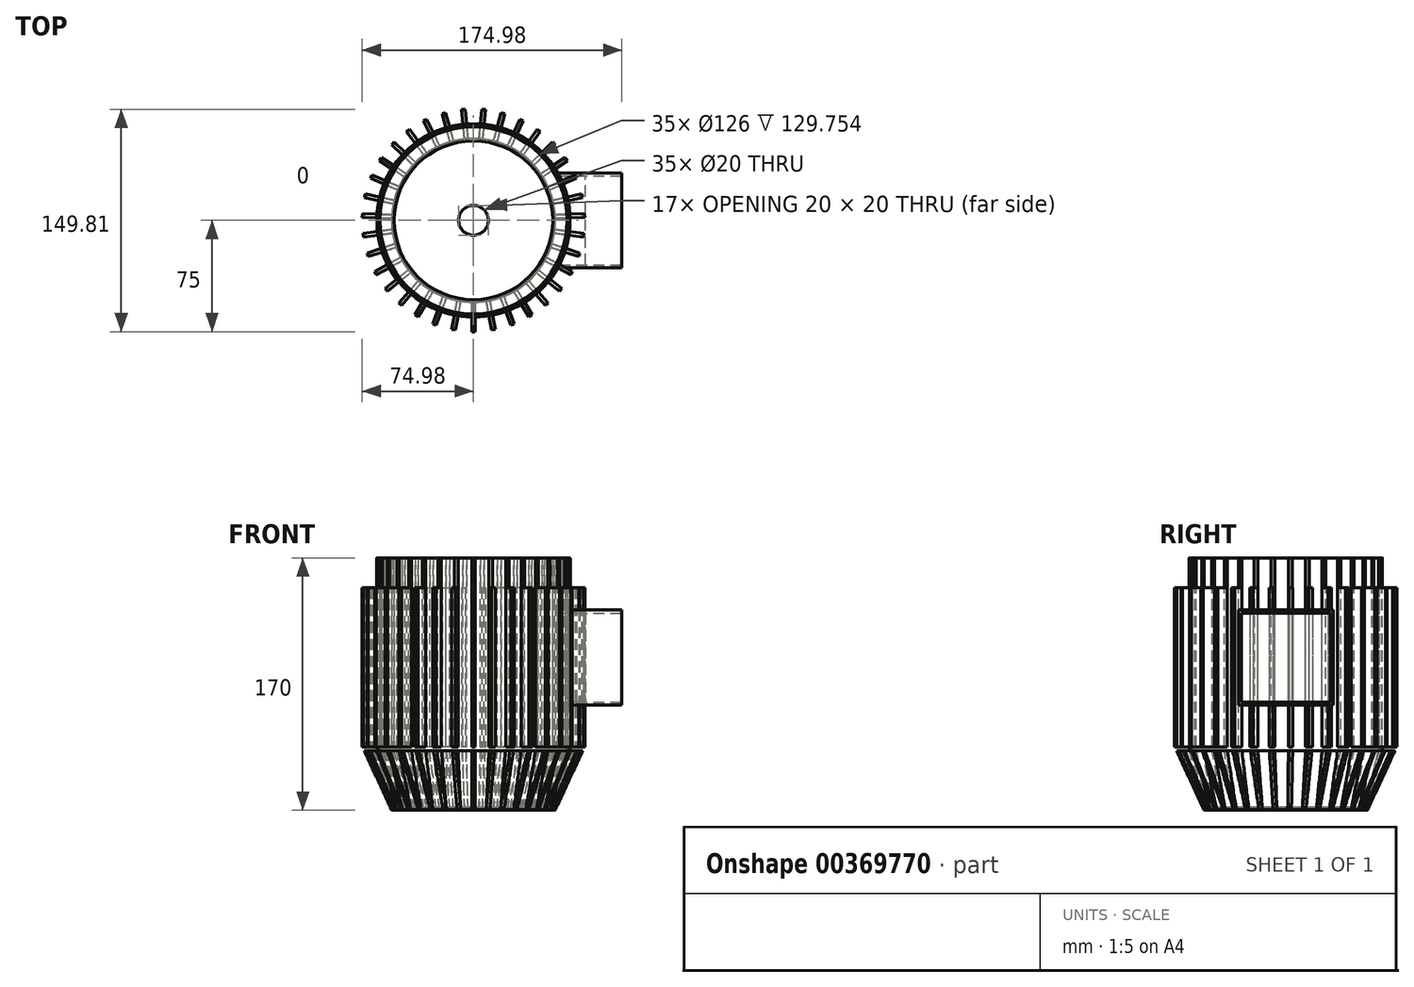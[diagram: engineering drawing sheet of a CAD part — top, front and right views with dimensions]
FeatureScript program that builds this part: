
annotation { "Feature Type Name" : "Feature", "Feature Type Description" : "" }
export const myFeature = defineFeature(function(context is Context, id is Id, definition is map)
    precondition{}
    {
        {
            var Q0;
            Q0=qCreatedBy(makeId("Top.planeOp"),FACE);
            var sketch = newSketch(context, id + "F0", { "sketchPlane" : qUnion([Q0])});
            skCircle(sketch, "E0", {"center": v(0, 0) * mm, "radius": 65 * mm});
            skSolve(sketch);
        }
        {
            var Q0;
            Q0=makeQuery(id+"F0.imprint","IMPRINT",FACE,{"disambiguationData":[TD([[makeQuery(id+"F0.imprint","IMPRINT",EDGE,{"derivedFrom":sQuery(id+"F0.wireOp",EDGE,"E0")}),1.0]])]});
            extrude(context, id + "F1", {"entities" : qUnion([Q0]), "oppositeDirection" : true, "depth" : 170 * mm, "offsetDistance" : 25 * mm});
        }
        {
            var Q0;
            Q0=makeQuery(id+"F1.opExtrude","CAP_FACE",FACE,{"disambiguationData":[OSD([sQuery(id+"F0.wireOp",EDGE,"E0")])],"isStart":false});
            chamfer(context, id + "F2", {"entities" : qUnion([Q0]), "chamferType" : ChamferType.TWO_OFFSETS, "width1" : 10 * mm, "oppositeDirection" : true, "width2" : 40 * mm, "tangentPropagation" : true});
        }
        {
            var Q0;
            Q0=makeQuery(id+"F1.opExtrude","CAP_FACE",FACE,{"disambiguationData":[OSD([sQuery(id+"F0.wireOp",EDGE,"E0")])],"isStart":true});
            shell(context, id + "F3", {"entities" : qUnion([Q0]), "thickness" : 2 * mm});
        }
        {
            var Q0;
            Q0=qCreatedBy(makeId("Front.planeOp"),FACE);
            cPlane(context, id + "F4", {"entities" : qUnion([Q0]), "cplaneType" : CPlaneType.OFFSET, "offset" : 75 * mm, "width" : 150 * mm, "height" : 150 * mm});
        }
        {
            var Q0;
            Q0=qCreatedBy(id+"F4.planeOp",FACE);
            var sketch = newSketch(context, id + "F5", { "sketchPlane" : qUnion([Q0])});
            skLineSegment(sketch, "E1.bottom", {"start": v(-1.25, 0) * mm, "end": v(1.25, 0) * mm});
            skLineSegment(sketch, "E1.top", {"start": v(-1.25, -170) * mm, "end": v(1.25, -170) * mm});
            skLineSegment(sketch, "E1.left", {"start": v(-1.25, 0) * mm, "end": v(-1.25, -170) * mm});
            skLineSegment(sketch, "E1.right", {"start": v(1.25, 0) * mm, "end": v(1.25, -170) * mm});
            skPoint(sketch, "E2.endSnap0", {"position": v(0, 0) * mm});
            skSolve(sketch);
        }
        {
            var Q0;
            Q0 = qSketchRegion(id + "F5", true);
            extrude(context, id + "F6", {"entities" : qUnion([Q0]), "operationType" : NewBodyOperationType.ADD, "endBound" : BoundingType.UP_TO_NEXT, "oppositeDirection" : true, "depth" : 22.5 * mm, "offsetDistance" : 25 * mm});
        }
        {
            var Q0;
            Q0=makeQuery(id+"F1.opExtrude","SWEPT_BODY",BODY,{"disambiguationData":[OSD([sQuery(id+"F0.wireOp",EDGE,"E0")])]});
            var Q1;
            Q1=makeQuery(id+"F1.opExtrude","SWEPT_FACE",FACE,{"disambiguationData":[OSD([sQuery(id+"F0.wireOp",EDGE,"E0")])]});
            circularPattern(context, id + "F7", {"entities" : qUnion([Q0]), "axis" : qUnion([Q1]), "angle" : 360 * degree, "instanceCount" : 35, "equalSpace" : true});
        }
        {
            var Q0;
            Q0=qCreatedBy(makeId("Front.planeOp"),FACE);
            var sketch = newSketch(context, id + "F8", { "sketchPlane" : qUnion([Q0])});
            skLineSegment(sketch, "E3", {"start": v(-54.94, -169.96) * mm, "end": v(-73.62, -129.74) * mm});
            skLineSegment(sketch, "E4", {"start": v(-80.72, -176.26) * mm, "end": v(-80.72, -127.24) * mm});
            skLineSegment(sketch, "E5", {"start": v(-80.72, -127.24) * mm, "end": v(-65, -127.24) * mm});
            skLineSegment(sketch, "E6", {"start": v(-73.62, -129.74) * mm, "end": v(-65, -129.74) * mm});
            skLineSegment(sketch, "E7", {"start": v(-65, -129.74) * mm, "end": v(-65, -127.24) * mm});
            skLineSegment(sketch, "E8", {"start": v(-80.72, -176.26) * mm, "end": v(-54.94, -169.96) * mm});
            skLineSegment(sketch, "E9", {"start": v(0, -180.24) * mm, "end": v(0, 21.57) * mm, "construction": true});
            skSolve(sketch);
        }
        {
            var Q0;
            Q0 = qSketchRegion(id + "F8", true);
            var Q1;
            Q1=sQuery(id+"F8.wireOp",EDGE,"E9");
            var Q2;
            Q2=sQuery(id+"F8.wireOp",EDGE,"E9");
            revolve(context, id + "F9", {"operationType" : NewBodyOperationType.REMOVE, "entities" : qUnion([Q0]), "surfaceEntities" : qUnion([Q1]), "axis" : qUnion([Q2]), "revolveType" : RevolveType.FULL, "oppositeDirection" : true});
        }
        {
            var Q0;
            Q0=makeQuery(id+"F7.opPattern","COPY",FACE,{"derivedFrom":makeQuery(id+"F6.boolean.opBoolean","MERGE",FACE,{"derivedFrom":[makeQuery(id+"F1.opExtrude","CAP_FACE",FACE,{"disambiguationData":[OSD([sQuery(id+"F0.wireOp",EDGE,"E0")])],"isStart":false}),makeQuery(id+"F6.opExtrude","SWEPT_FACE",FACE,{"disambiguationData":[OSD([sQuery(id+"F5.wireOp",EDGE,"E1.top")])]})]}),"instanceName":"17"});
            var sketch = newSketch(context, id + "F10", { "sketchPlane" : qUnion([Q0])});
            skCircle(sketch, "E10", {"center": v(0, 0) * mm, "radius": 10 * mm});
            skSolve(sketch);
        }
        {
            var Q0;
            Q0 = qSketchRegion(id + "F10", true);
            extrude(context, id + "F11", {"entities" : qUnion([Q0]), "operationType" : NewBodyOperationType.REMOVE, "endBound" : BoundingType.THROUGH_ALL, "oppositeDirection" : true, "depth" : 25 * mm, "offsetDistance" : 25 * mm});
        }
        {
            var Q0;
            Q0=qCreatedBy(makeId("Right.planeOp"),FACE);
            cPlane(context, id + "F12", {"entities" : qUnion([Q0]), "cplaneType" : CPlaneType.OFFSET, "offset" : 100 * mm, "width" : 150 * mm, "height" : 150 * mm});
        }
        {
            var Q0;
            Q0=qCreatedBy(id+"F12.planeOp",FACE);
            var sketch = newSketch(context, id + "F13", { "sketchPlane" : qUnion([Q0])});
            skLineSegment(sketch, "E11.bottom", {"start": v(-30, -37.24) * mm, "end": v(30, -37.24) * mm});
            skLineSegment(sketch, "E11.top", {"start": v(-30, -97.24) * mm, "end": v(30, -97.24) * mm});
            skLineSegment(sketch, "E11.left", {"start": v(-30, -37.24) * mm, "end": v(-30, -97.24) * mm});
            skLineSegment(sketch, "E11.right", {"start": v(30, -37.24) * mm, "end": v(30, -97.24) * mm});
            skLineSegment(sketch, "E12", {"start": v(0, 0) * mm, "end": v(0, -219.43) * mm});
            skLineSegment(sketch, "E13", {"start": v(0, -219.43) * mm, "end": v(0, -207.66) * mm});
            skLineSegment(sketch, "E14.bottom", {"start": v(-32, -35.08) * mm, "end": v(32, -35.08) * mm});
            skLineSegment(sketch, "E14.top", {"start": v(-32, -99.08) * mm, "end": v(32, -99.08) * mm});
            skLineSegment(sketch, "E14.left", {"start": v(-32, -35.08) * mm, "end": v(-32, -99.08) * mm});
            skLineSegment(sketch, "E14.right", {"start": v(32, -35.08) * mm, "end": v(32, -99.08) * mm});
            skSolve(sketch);
        }
        {
            var Q0;
            Q0=makeQuery(id+"F13.imprint","IMPRINT",FACE,{"disambiguationData":[TD([[makeQuery(id+"F13.imprint","IMPRINT",EDGE,{"derivedFrom":sQuery(id+"F13.wireOp",EDGE,"E11.bottom")}),-1.0]])]});
            extrude(context, id + "F14", {"entities" : qUnion([Q0]), "endBound" : BoundingType.UP_TO_NEXT, "oppositeDirection" : true, "depth" : 25 * mm, "offsetDistance" : 25 * mm});
        }
        {
            var Q0;
            Q0 = qSketchRegion(id + "F13", true);
            extrude(context, id + "F15", {"entities" : qUnion([Q0]), "endBound" : BoundingType.UP_TO_NEXT, "oppositeDirection" : true, "depth" : 25 * mm, "offsetDistance" : 25 * mm});
        }
        {
            var Q0;
            Q0=makeQuery(id+"F14.opExtrude","CAP_FACE",FACE,{"disambiguationData":[OSD([sQuery(id+"F13.wireOp",EDGE,"E11.bottom"),sQuery(id+"F13.wireOp",EDGE,"E11.top"),sQuery(id+"F13.wireOp",EDGE,"E11.left"),sQuery(id+"F13.wireOp",EDGE,"E11.right")])],"isStart":true});
            extrude(context, id + "F16", {"entities" : qUnion([Q0]), "operationType" : NewBodyOperationType.REMOVE, "oppositeDirection" : true, "depth" : 24.5 * mm, "offsetDistance" : 25 * mm});
        }
        {
            var Q0;
            Q0=qCreatedBy(makeId("Right.planeOp"),FACE);
            var sketch = newSketch(context, id + "F17", { "sketchPlane" : qUnion([Q0])});
            skLineSegment(sketch, "E15", {"start": v(0, 84.45) * mm, "end": v(0, -186.53) * mm, "construction": true});
            skLineSegment(sketch, "E16.bottom", {"start": v(-84.61, 0) * mm, "end": v(-65.15, 0) * mm});
            skLineSegment(sketch, "E16.top", {"start": v(-84.61, -20) * mm, "end": v(-65.15, -20) * mm});
            skLineSegment(sketch, "E16.left", {"start": v(-84.61, 0) * mm, "end": v(-84.61, -20) * mm});
            skLineSegment(sketch, "E16.right", {"start": v(-65.15, 0) * mm, "end": v(-65.15, -20) * mm});
            skSolve(sketch);
        }
        {
            var Q0;
            Q0=makeQuery(id+"F17.imprint","IMPRINT",FACE,{"disambiguationData":[TD([[makeQuery(id+"F17.imprint","IMPRINT",EDGE,{"derivedFrom":sQuery(id+"F17.wireOp",EDGE,"E16.bottom")}),-1.0]])]});
            var Q1;
            Q1=sQuery(id+"F17.wireOp",EDGE,"E15");
            revolve(context, id + "F18", {"operationType" : NewBodyOperationType.REMOVE, "entities" : qUnion([Q0]), "axis" : qUnion([Q1]), "revolveType" : RevolveType.FULL, "oppositeDirection" : true});
        }
    });
